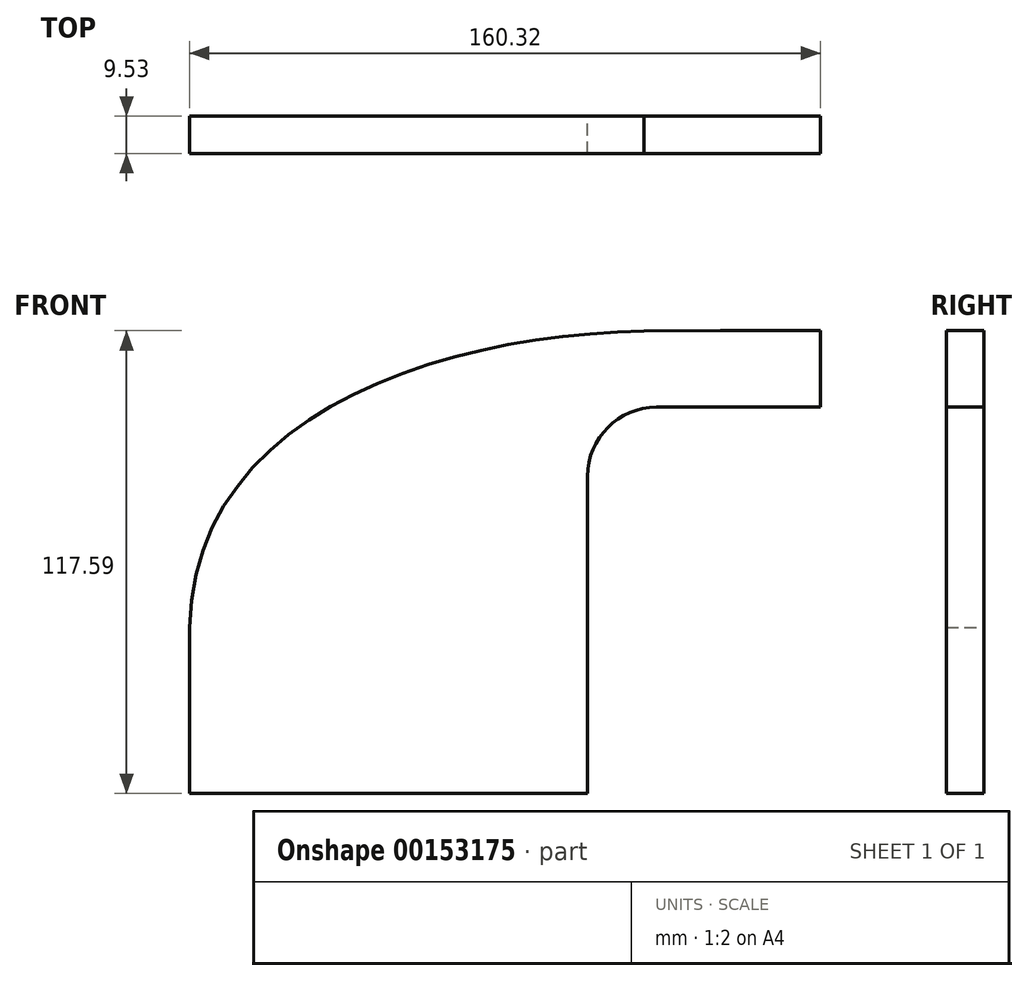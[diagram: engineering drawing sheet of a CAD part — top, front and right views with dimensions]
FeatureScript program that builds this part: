
annotation { "Feature Type Name" : "Feature", "Feature Type Description" : "" }
export const myFeature = defineFeature(function(context is Context, id is Id, definition is map)
    precondition{}
    {
        {
            var Q0;
            Q0=qCreatedBy(makeId("Front.planeOp"),FACE);
            var sketch = newSketch(context, id + "F0", { "sketchPlane" : qUnion([Q0])});
            skLineSegment(sketch, "E0.bottom", {"start": v(-50.58, 21.07) * mm, "end": v(50.58, 21.07) * mm});
            skLineSegment(sketch, "E0.top", {"start": v(-50.58, -21.07) * mm, "end": v(50.58, -21.07) * mm});
            skLineSegment(sketch, "E0.left", {"start": v(-50.58, 21.07) * mm, "end": v(-50.58, -21.07) * mm});
            skLineSegment(sketch, "E0.right", {"start": v(50.58, 21.07) * mm, "end": v(50.58, -21.07) * mm});
            skPoint(sketch, "E0.middle", {"position": v(0, 0) * mm});
            skPoint(sketch, "E1.middle", {"position": v(97.04, 86.8) * mm});
            skPoint(sketch, "E1.left.start.orphan", {"position": v(109.74, 77.06) * mm});
            skPoint(sketch, "E1.top.start.orphan", {"position": v(109.74, 96.52) * mm});
            skPoint(sketch, "E1.right.end.orphan", {"position": v(84.34, 96.52) * mm});
            skPoint(sketch, "E2.end.orphan", {"position": v(84.34, 77.06) * mm});
            skLineSegment(sketch, "E3", {"start": v(84.34, 77.06) * mm, "end": v(84.34, 96.52) * mm});
            skLineSegment(sketch, "E4", {"start": v(84.34, 96.52) * mm, "end": v(109.74, 96.52) * mm});
            skLineSegment(sketch, "E5", {"start": v(109.74, 96.52) * mm, "end": v(109.74, 77.06) * mm});
            skLineSegment(sketch, "E6", {"start": v(84.34, 77.06) * mm, "end": v(109.74, 77.06) * mm});
            skLineSegment(sketch, "E7", {"start": v(50.58, 21.07) * mm, "end": v(50.58, 59.53) * mm});
            skArc(sketch, "E8", {"start": v(50.58, 59.53) * mm, "mid": v(55.7, 71.93) * mm, "end": v(68.1, 77.06) * mm});
            skLineSegment(sketch, "E9", {"start": v(68.1, 77.06) * mm, "end": v(84.34, 77.06) * mm});
            skLineSegment(sketch, "E10.0", {"start": v(64.96, 96.32) * mm, "end": v(64.96, 96.44) * mm});
            skArc(sketch, "E10.1", {"start": v(31.19, 59.53) * mm, "mid": v(40.9, 84.5) * mm, "end": v(64.96, 96.32) * mm});
            skLineSegment(sketch, "E10.2", {"start": v(31.19, 21.07) * mm, "end": v(31.19, 59.53) * mm});
            skLineSegment(sketch, "E11", {"start": v(64.96, 96.44) * mm, "end": v(84.34, 96.52) * mm});
            skFitSpline(sketch, "E12", {"points": [v(64.96, 96.44) * mm, v(-50.58, 21.07) * mm], "startDerivative": vector(-155.65, -3.22) * mm, "endDerivative": vector(-3.49, -163.91) * mm});
            skSolve(sketch);
        }
        {
            var Q0;
            Q0=makeQuery(id+"F0.imprint","IMPRINT",FACE,{"disambiguationData":[TD([[makeQuery(id+"F0.imprint","IMPRINT",EDGE,{"derivedFrom":sQuery(id+"F0.wireOp",EDGE,"E3")}),1.0]])]});
            var Q1;
            Q1=makeQuery(id+"F0.imprint","IMPRINT",FACE,{"disambiguationData":[TD([[makeQuery(id+"F0.imprint","IMPRINT",EDGE,{"derivedFrom":sQuery(id+"F0.wireOp",EDGE,"E0.top")}),1.0]])]});
            var Q2;
            Q2=makeQuery(id+"F0.imprint","IMPRINT",FACE,{"disambiguationData":[TD([[makeQuery(id+"F0.imprint","IMPRINT",EDGE,{"derivedFrom":sQuery(id+"F0.wireOp",EDGE,"E10.0")}),1.0]])]});
            var Q3;
            Q3=makeQuery(id+"F0.imprint","IMPRINT",FACE,{"disambiguationData":[TD([[makeQuery(id+"F0.imprint","IMPRINT",EDGE,{"derivedFrom":sQuery(id+"F0.wireOp",EDGE,"E3")}),-1.0]])]});
            extrude(context, id + "F1", {"entities" : qUnion([Q0, Q1, Q2, Q3]), "depth" : 9.52 * mm});
        }
    });
